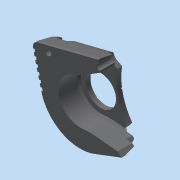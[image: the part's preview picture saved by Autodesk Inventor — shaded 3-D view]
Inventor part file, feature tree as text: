
AUTODESK INVENTOR PART (.ipt)
format: ipt  version: 2014 SP1 (Build 180222100, 222)  size: 396,288 bytes
history: native  units: in
note: dims shown in document units (in); Inventor stores cm internally (conversion verified against a paired STEP export)
features: sketch x8, extrude x8, chamfer x5, fillet x2, projected_geometry x2, other x1, pattern_circular x1
ambient origin geometry x8: Origin, YZ Plane, XZ Plane, XY Plane, X Axis, Y Axis, Z Axis, Center Point
bodies: Solid1 (feature_tree)
feature tree (27):
  other  "mount_alt.ipt"
  sketch  "Sketch2"  dims[d0=0.3937in d1=0.1181in d2=0.2362in]
  extrude  "Extrusion1"  Depth=0.3937in
  fillet  "Fillet3"  Radius=0.2362in
  extrude  "Extrusion7"  Depth=0.6693in TaperAngle=0.0deg
  chamfer  "Chamfer6"  Distance=0.1575in
  chamfer  "Chamfer14"  Distance=0.1in Angle=45.0deg
  extrude  "Extrusion9"  Depth=0.201in
  extrude  "Extrusion10"  Depth=0.3937in
  extrude  "Extrusion12"  Depth=0.3937in
  fillet  "Fillet10"  Radius=0.1969in
  extrude  "Extrusion17"  Depth=0.3937in
  chamfer  "Chamfer16"  Distance=0.3543in
  chamfer  "Chamfer17"  Distance=0.1969in
  chamfer  "Chamfer18"  Distance=0.5906in
  extrude  "Extrusion18"  Depth=0.0394in
  extrude  "Extrusion15"  TaperAngle=150.0deg  [1 undecoded]
  pattern_circular  "Circular Pattern1"  [2 undecoded]
  sketch  "Sketch22"  dims[d66=0.1181in d67=0.0in d68=0.425in d69=0.425in d70=0.1969in d71=0.0in d81=0.1181in d82=0.3543in d83=0.0in d98=0.1969in d115=0.5906in d116=0.0394in d117=150.0deg d118=0.0197in d119=0.0in d120=1.9685in d121=360.0deg d125=0.0591in d126=0.125in d127=45.0deg d128=0.0in d129=0.0in d130=0.1772in d131=0.1in d132=2.3622in d134=0.2in d135=0.3937in d137=1.0in d139=0.05in d140=0.0in d144=0.17in d145=0.125in d146=45.0deg d148=0.2in d149=0.125in d150=45.0deg d151=0.2in d152=0.125in d153=45.0deg]
  sketch  "Sketch6"  dims[d3=0.1772in d5=0.6693in d6=0.0in]
  sketch  "Sketch9"  dims[d31=1.6914in]
  sketch  "Sketch10"  dims[d32=3.5433in]
  sketch  "Sketch12"  dims[d42=0.315in]
  sketch  "Sketch14"  dims[d43=0.9843in d44=0.1575in d45=0.0in d46=0.1in d47=0.125in d48=45.0deg]
  projected_geometry  "Projected Loop2"
  projected_geometry  "Projected Loop4"
  sketch  "Sketch18"  dims[d64=0.201in d65=0.201in]
note: 3 required parameter values undecoded (feature->parameter linkage not recoverable at this tier; creation-order binding heuristic only, values carry confidence <= 0.55)
